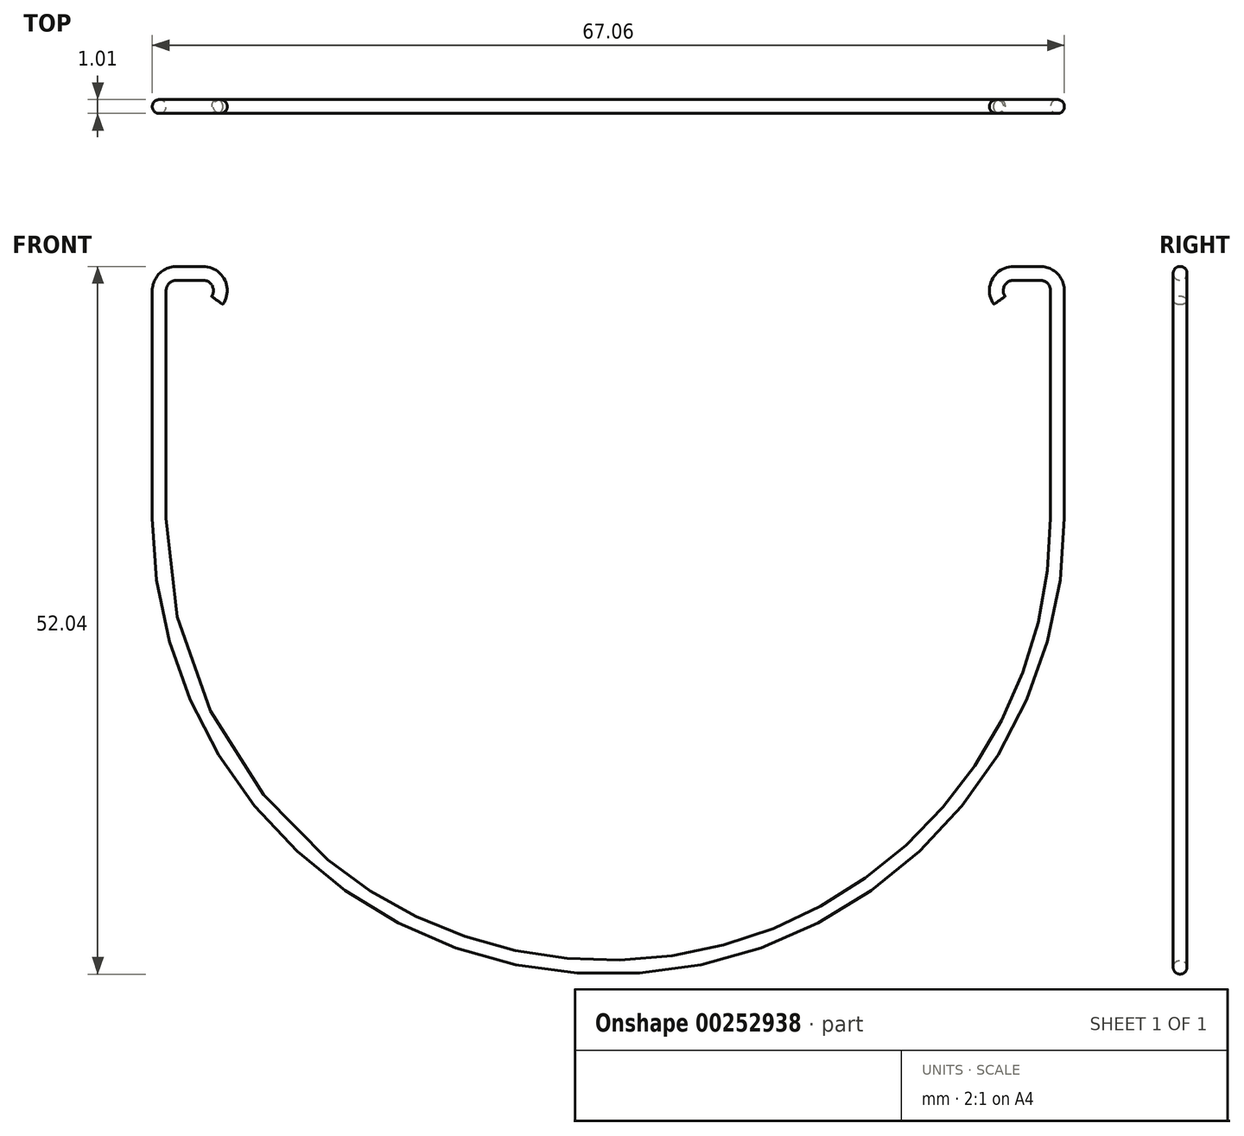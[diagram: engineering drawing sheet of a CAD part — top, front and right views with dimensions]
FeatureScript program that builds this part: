
annotation { "Feature Type Name" : "Feature", "Feature Type Description" : "" }
export const myFeature = defineFeature(function(context is Context, id is Id, definition is map)
    precondition{}
    {
        {
            var Q0;
            Q0=qCreatedBy(makeId("Front.planeOp"),FACE);
            cPlane(context, id + "F0", {"entities" : qUnion([Q0]), "cplaneType" : CPlaneType.OFFSET, "offset" : 20.95 * mm, "width" : 152.4 * mm, "height" : 152.4 * mm});
        }
        {
            var Q0;
            Q0=qCreatedBy(id+"F0.planeOp",FACE);
            var sketch = newSketch(context, id + "F1", { "sketchPlane" : qUnion([Q0])});
            skArc(sketch, "E0", {"start": v(0, 15.65) * mm, "mid": v(23.35, 25.32) * mm, "end": v(33.02, 48.67) * mm});
            skLineSegment(sketch, "E1", {"start": v(33.02, 48.67) * mm, "end": v(33.02, 65.4) * mm});
            skLineSegment(sketch, "E2", {"start": v(31.75, 66.68) * mm, "end": v(29.8, 66.68) * mm});
            skPoint(sketch, "E3.orphan", {"position": v(0, 13.74) * mm});
            skPoint(sketch, "E4.visualSharp", {"position": v(33.02, 66.68) * mm});
            skArc(sketch, "E4.filletArc", {"start": v(33.02, 65.4) * mm, "mid": v(32.65, 66.3) * mm, "end": v(31.75, 66.68) * mm});
            skArc(sketch, "E5", {"start": v(29.8, 66.68) * mm, "mid": v(28.67, 66) * mm, "end": v(28.75, 64.68) * mm});
            skPoint(sketch, "E6.orphan", {"position": v(28.58, 66.68) * mm});
            skPoint(sketch, "E7.MirrorCS.end.orphan", {"position": v(-33.02, 48.67) * mm});
            skPoint(sketch, "E7.MirrorCS.start.orphan", {"position": v(0, 15.65) * mm});
            skSolve(sketch);
        }
        {
            var Q0;
            Q0=qCreatedBy(makeId("Right.planeOp"),FACE);
            var sketch = newSketch(context, id + "F2", { "sketchPlane" : qUnion([Q0])});
            skCircle(sketch, "E8", {"center": v(-20.96, 15.65) * mm, "radius": 0.5 * mm});
            skSolve(sketch);
        }
        {
            var Q0;
            Q0=makeQuery(id+"F2.imprint","IMPRINT",FACE,{"disambiguationData":[TD([[makeQuery(id+"F2.imprint","IMPRINT",EDGE,{"derivedFrom":sQuery(id+"F2.wireOp",EDGE,"E8")}),1.0]])]});
            var Q1;
            Q1=sQuery(id+"F1.wireOp",EDGE,"E0");
            var Q2;
            Q2=sQuery(id+"F1.wireOp",EDGE,"E1");
            var Q3;
            Q3=sQuery(id+"F1.wireOp",EDGE,"E4.filletArc");
            var Q4;
            Q4=sQuery(id+"F1.wireOp",EDGE,"E2");
            var Q5;
            Q5=sQuery(id+"F1.wireOp",EDGE,"E5");
            sweep(context, id + "F3", {"profiles" : qUnion([Q0]), "path" : qUnion([Q1, Q2, Q3, Q4, Q5])});
        }
        {
            var Q0;
            Q0=makeQuery(id+"F3.opSweep","SWEPT_BODY",BODY,{"disambiguationData":[OSD([sQuery(id+"F1.wireOp",EDGE,"E5"),sQuery(id+"F2.wireOp",EDGE,"E8")])]});
            var Q1;
            Q1=qCreatedBy(makeId("Right.planeOp"),FACE);
            mirror(context, id + "F4", {"operationType" : NewBodyOperationType.ADD, "entities" : qUnion([Q0]), "mirrorPlane" : qUnion([Q1])});
        }
        {
            var Q0;
            Q0=qCreatedBy(id+"F0.planeOp",FACE);
            var sketch = newSketch(context, id + "F5", { "sketchPlane" : qUnion([Q0])});
            skLineSegment(sketch, "E9", {"start": v(0, 66.68) * mm, "end": v(0, 0) * mm, "construction": true});
            skPoint(sketch, "E10", {"position": v(29.8, 66.68) * mm});
            skSolve(sketch);
        }
        {
            var Q0;
            Q0=makeQuery(id+"F3.opSweep","SWEPT_BODY",BODY,{"disambiguationData":[OSD([sQuery(id+"F1.wireOp",EDGE,"E5"),sQuery(id+"F2.wireOp",EDGE,"E8")])]});
            var Q1;
            Q1=sQuery(id+"F5.wireOp",EDGE,"E9");
            transform(context, id + "F6", {"entities" : qUnion([Q0]), "transformType" : TransformType.TRANSLATION_ENTITY, "oppositeDirectionEntity" : false, "transformLine" : qUnion([Q1]), "makeCopy" : false});
        }
    });
